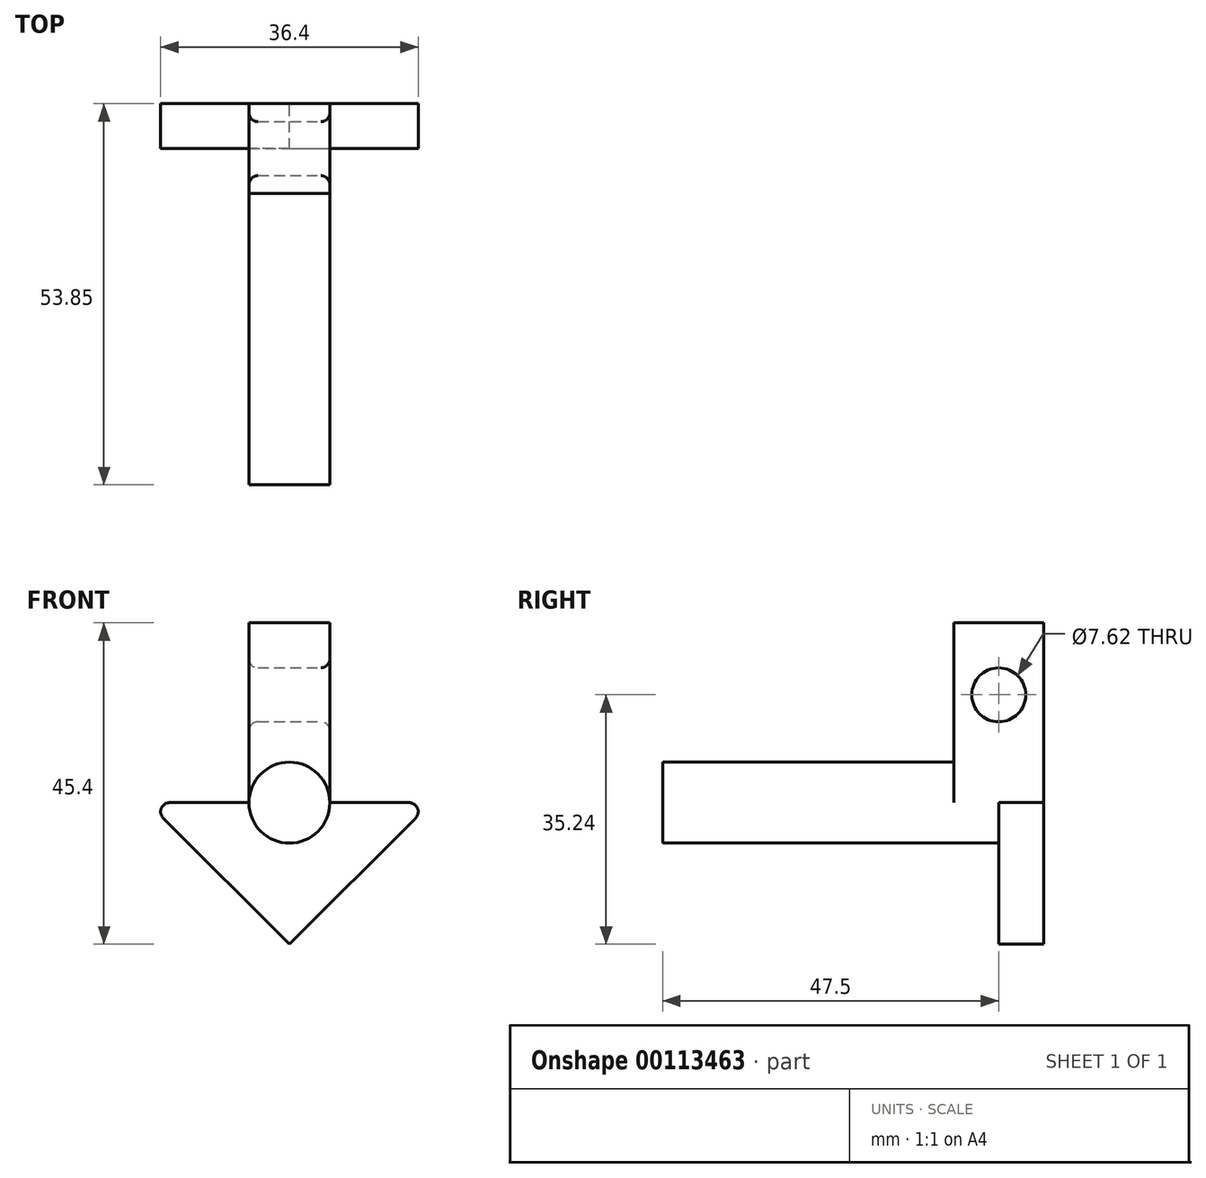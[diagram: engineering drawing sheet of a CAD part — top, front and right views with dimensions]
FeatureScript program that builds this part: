
annotation { "Feature Type Name" : "Feature", "Feature Type Description" : "" }
export const myFeature = defineFeature(function(context is Context, id is Id, definition is map)
    precondition{}
    {
        {
            var Q0;
            Q0=qCreatedBy(makeId("Front.planeOp"),FACE);
            var sketch = newSketch(context, id + "F0", { "sketchPlane" : qUnion([Q0])});
            skLineSegment(sketch, "E0", {"start": v(0, 0) * mm, "end": v(0, 20) * mm, "construction": true});
            skLineSegment(sketch, "E1", {"start": v(0, 0) * mm, "end": v(20, 20) * mm});
            skLineSegment(sketch, "E2", {"start": v(0, 0) * mm, "end": v(-20, 20) * mm});
            skLineSegment(sketch, "E3", {"start": v(-20, 20) * mm, "end": v(20, 20) * mm});
            skCircle(sketch, "E4", {"center": v(0, 20) * mm, "radius": 5.72 * mm});
            skLineSegment(sketch, "E5", {"start": v(-5.72, 20) * mm, "end": v(-5.72, 45.4) * mm});
            skLineSegment(sketch, "E6", {"start": v(-5.72, 45.4) * mm, "end": v(5.71, 45.4) * mm});
            skLineSegment(sketch, "E7", {"start": v(5.71, 45.4) * mm, "end": v(5.71, 20) * mm});
            skSolve(sketch);
        }
        {
            var Q0;
            {var subQ1=sQuery(id+"F0.wireOp",EDGE,"E1");Q0=makeQuery(id+"F0.imprint","IMPRINT",FACE,{"disambiguationData":[TD([[makeQuery(id+"F0.imprint","IMPRINT",EDGE,{"derivedFrom":subQ1}),1.0]])]});}
            extrude(context, id + "F1", {"entities" : qUnion([Q0]), "depth" : 6.35 * mm});
        }
        {
            var Q0;
            {var subQ0=sQuery(id+"F0.wireOp",EDGE,"E4");var subQ1=sQuery(id+"F0.wireOp",EDGE,"E3");var subQ2=makeQuery(id+"F0.imprint","INTERSECT",VERTEX,{"derivedFrom":[subQ1,subQ0,sQuery(id+"F0.wireOp",EDGE,"E5")]});Q0=makeQuery(id+"F0.imprint","IMPRINT",FACE,{"disambiguationData":[TD([[makeQuery(id+"F0.imprint","IMPRINT",EDGE,{"disambiguationData":[TD([[subQ2,-1.0]])],"derivedFrom":subQ1}),-1.0]])]});}
            var Q1;
            {var subQ0=sQuery(id+"F0.wireOp",EDGE,"E4");var subQ1=sQuery(id+"F0.wireOp",EDGE,"E3");var subQ2=makeQuery(id+"F0.imprint","INTERSECT",VERTEX,{"derivedFrom":[subQ1,subQ0,sQuery(id+"F0.wireOp",EDGE,"E5")]});Q1=makeQuery(id+"F0.imprint","IMPRINT",FACE,{"disambiguationData":[TD([[makeQuery(id+"F0.imprint","IMPRINT",EDGE,{"disambiguationData":[TD([[subQ2,-1.0]])],"derivedFrom":subQ1}),1.0]])]});}
            extrude(context, id + "F2", {"entities" : qUnion([Q0, Q1]), "operationType" : NewBodyOperationType.ADD, "depth" : 53.85 * mm});
        }
        {
            var Q0;
            {var subQ0=sQuery(id+"F0.wireOp",EDGE,"E5");Q0=makeQuery(id+"F0.imprint","IMPRINT",FACE,{"disambiguationData":[TD([[makeQuery(id+"F0.imprint","IMPRINT",EDGE,{"derivedFrom":subQ0}),-1.0]])]});}
            extrude(context, id + "F3", {"entities" : qUnion([Q0]), "operationType" : NewBodyOperationType.ADD, "depth" : 12.7 * mm});
        }
        {
            var Q0;
            Q0=makeQuery(id+"F3.opExtrude","SWEPT_FACE",FACE,{"disambiguationData":[OSD([sQuery(id+"F0.wireOp",EDGE,"E7")])]});
            cPlane(context, id + "F4", {"entities" : qUnion([Q0]), "cplaneType" : CPlaneType.OFFSET, "offset" : 25.4 * mm, "width" : 152.4 * mm, "height" : 152.4 * mm});
        }
        {
            var Q0;
            Q0=qCreatedBy(id+"F4.planeOp",FACE);
            var sketch = newSketch(context, id + "F5", { "sketchPlane" : qUnion([Q0])});
            skLineSegment(sketch, "E8.0.0", {"start": v(0, 20) * mm, "end": v(0, 45.4) * mm});
            skLineSegment(sketch, "E8.0.1", {"start": v(0, 45.4) * mm, "end": v(-12.7, 45.4) * mm});
            skLineSegment(sketch, "E8.0.2", {"start": v(-12.7, 45.4) * mm, "end": v(-12.7, 20) * mm});
            skLineSegment(sketch, "E8.0.3", {"start": v(-12.7, 20) * mm, "end": v(-6.35, 20) * mm});
            skLineSegment(sketch, "E8.0.4", {"start": v(-6.35, 20) * mm, "end": v(0, 20) * mm});
            skCircle(sketch, "E9", {"center": v(-6.35, 35.24) * mm, "radius": 3.81 * mm});
            skLineSegment(sketch, "E10", {"start": v(-6.35, 20) * mm, "end": v(-6.35, 45.4) * mm, "construction": true});
            skSolve(sketch);
        }
        {
            var Q0;
            Q0=makeQuery(id+"F5.imprint","IMPRINT",FACE,{"disambiguationData":[TD([[makeQuery(id+"F5.imprint","IMPRINT",EDGE,{"derivedFrom":sQuery(id+"F5.wireOp",EDGE,"E9")}),1.0]])]});
            extrude(context, id + "F6", {"entities" : qUnion([Q0]), "operationType" : NewBodyOperationType.REMOVE, "endBound" : BoundingType.THROUGH_ALL, "oppositeDirection" : true, "depth" : 25.4 * mm});
        }
        {
            var Q0;
            Q0=makeQuery(id+"F6.boolean.opBoolean","INTERSECT",EDGE,{"derivedFrom":[makeQuery(id+"F3.opExtrude","SWEPT_FACE",FACE,{"disambiguationData":[OSD([sQuery(id+"F0.wireOp",EDGE,"E7")])]}),makeQuery(id+"F6.opExtrude","SWEPT_FACE",FACE,{"disambiguationData":[OSD([sQuery(id+"F5.wireOp",EDGE,"E9")])]})]});
            var Q1;
            Q1=makeQuery(id+"F6.boolean.opBoolean","INTERSECT",EDGE,{"derivedFrom":[makeQuery(id+"F3.opExtrude","SWEPT_FACE",FACE,{"disambiguationData":[OSD([sQuery(id+"F0.wireOp",EDGE,"E5")])]}),makeQuery(id+"F6.opExtrude","SWEPT_FACE",FACE,{"disambiguationData":[OSD([sQuery(id+"F5.wireOp",EDGE,"E9")])]})]});
            fillet(context, id + "F7", {"entities" : qUnion([Q0, Q1]), "radius" : 1.27 * mm, "tangentPropagation" : true, "allowEdgeOverflow" : false});
        }
        {
            var Q0;
            Q0=makeQuery(id+"F1.opExtrude","SWEPT_EDGE",EDGE,{"disambiguationData":[OSD([sQuery(id+"F0.wireOp",EDGE,"E2"),sQuery(id+"F0.wireOp",EDGE,"E3")])]});
            var Q1;
            Q1=makeQuery(id+"F1.opExtrude","SWEPT_EDGE",EDGE,{"disambiguationData":[OSD([sQuery(id+"F0.wireOp",EDGE,"E1"),sQuery(id+"F0.wireOp",EDGE,"E3")])]});
            fillet(context, id + "F8", {"entities" : qUnion([Q0, Q1]), "radius" : 1.27 * mm, "tangentPropagation" : true, "allowEdgeOverflow" : false});
        }
    });
